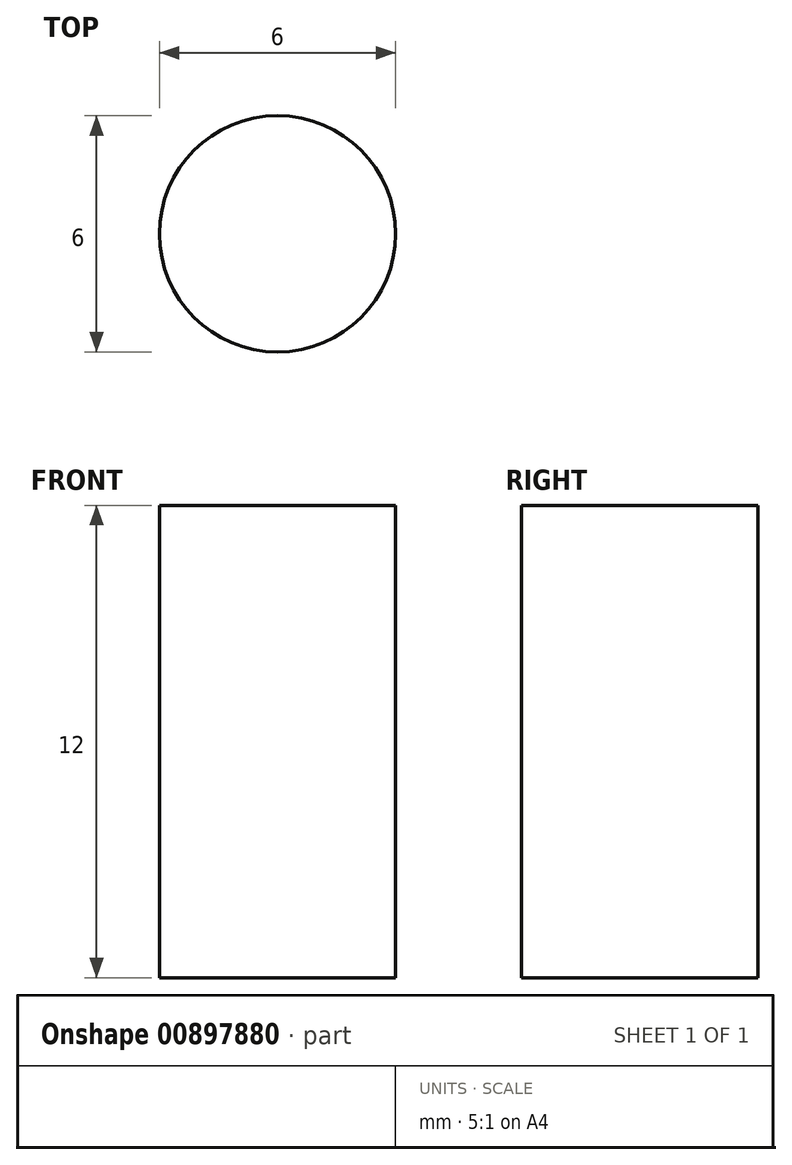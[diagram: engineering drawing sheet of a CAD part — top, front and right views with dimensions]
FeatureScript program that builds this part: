
annotation { "Feature Type Name" : "Feature", "Feature Type Description" : "" }
export const myFeature = defineFeature(function(context is Context, id is Id, definition is map)
    precondition{}
    {
        {
            var Q0;
            Q0=qCreatedBy(makeId("Top.planeOp"),FACE);
            var sketch = newSketch(context, id + "F0", { "sketchPlane" : qUnion([Q0])});
            skCircle(sketch, "E0", {"center": v(0, 0) * mm, "radius": 3 * mm});
            skSolve(sketch);
        }
        {
            var Q0;
            Q0=makeQuery(id+"F0.imprint","IMPRINT",FACE,{"disambiguationData":[TD([[makeQuery(id+"F0.imprint","IMPRINT",EDGE,{"derivedFrom":sQuery(id+"F0.wireOp",EDGE,"E0")}),1.0]])]});
            extrude(context, id + "F1", {"entities" : qUnion([Q0]), "depth" : 12 * mm, "offsetDistance" : 25 * mm});
        }
    });
